# Revit family: КСК_без стены_Eng
name_source: partatom
category: Mechanical Equipment
units: mm (PartAtom-declared; Revit-internal decimal feet)

## family parameters
Always vertical = Yes
Classification = None
Cut with Voids When Loaded = No
Part Type = Normal
Room Calculation Point = No
Round Connector Dimension = Use Diameter
Shared = No
Work Plane-Based = No

## types (24) — shared parameters
00_20_Manufacturer = Vents
00_20_Name = Centrifugal kitchen fan in sound-insulated casing
Casing Material = Steel, galvanized
Frequency = 50 Hz
Load Classification = HVAC
Maintenance zone material = <By Category>
Manufacturer = Vents
URL = https://ventilation-system.com
zero-valued in all types: Default Elevation

## per-type parameters (varying)
- KSK 150 4D: Amperage=1 A; B=410 mm; D=150 mm  [stored 0.492126 ft]; Diameter=150 mm  [stored 0.492126 ft]; Dy=145 mm  [stored 0.475722 ft]; H=540 mm; H1=365 mm; Height=540 mm; L=525 mm; L1=500 mm; L4=205 mm; Length=525 mm; Maximum Air Flow=730.0 m³/h; Motor=Motor : Motor_0.25 kW; Number of Fase=3; Power=180 W; Sound pressure level at 3 m distance=41 dBA; Voltage=400 V; Weight=17.00 kg; Width=410 mm; b=105 mm  [stored 0.344488 ft]; h1=32 mm  [stored 0.104987 ft]; l1=50 mm  [stored 0.164042 ft]; l2=73 mm; l3=133 mm  [stored 0.436352 ft]
- KSK 150 4E: Amperage=2 A; B=410 mm; D=150 mm  [stored 0.492126 ft]; Diameter=150 mm  [stored 0.492126 ft]; Dy=145 mm  [stored 0.475722 ft]; H=540 mm; H1=365 mm; Height=540 mm; L=525 mm; L1=500 mm; L4=205 mm; Length=525 mm; Maximum Air Flow=700.0 m³/h; Motor=Motor : Motor_0.25 kW; Number of Fase=1; Power=180 W; Sound pressure level at 3 m distance=41 dBA; Voltage=230 V; Weight=17.00 kg; Width=410 mm; b=105 mm  [stored 0.344488 ft]; h1=32 mm  [stored 0.104987 ft]; l1=50 mm  [stored 0.164042 ft]; l2=73 mm; l3=133 mm  [stored 0.436352 ft]
- KSK 450 6E: Amperage=3 A; B=996 mm; D=450 mm; Diameter=450 mm; Dy=445 mm; H=980 mm; H1=870 mm; Height=980 mm; L=925 mm; L1=900 mm; L4=437 mm; Length=925 mm; Maximum Air Flow=5299.0 m³/h; Motor=Motor : Motor_0.55 kW; Number of Fase=1; Power=594 W; Sound pressure level at 3 m distance=50 dBA; Voltage=230 V; Weight=105.00 kg; Width=996 mm; b=255 mm  [stored 0.836614 ft]; h1=36 mm  [stored 0.11811 ft]; l1=65 mm  [stored 0.213255 ft]; l2=189 mm; l3=249 mm
- KSK 160 4D: Amperage=1 A; B=410 mm; D=160 mm  [stored 0.524934 ft]; Diameter=160 mm  [stored 0.524934 ft]; Dy=155 mm  [stored 0.50853 ft]; H=540 mm; H1=365 mm; Height=540 mm; L=525 mm; L1=500 mm; L4=205 mm; Length=525 mm; Maximum Air Flow=730.0 m³/h; Motor=Motor : Motor_0.25 kW; Number of Fase=3; Power=180 W; Sound pressure level at 3 m distance=41 dBA; Voltage=400 V; Weight=17.00 kg; Width=410 mm; b=110 mm  [stored 0.360892 ft]; h1=32 mm  [stored 0.104987 ft]; l1=50 mm  [stored 0.164042 ft]; l2=73 mm; l3=133 mm  [stored 0.436352 ft]
- KSK 160 4E: Amperage=2 A; B=410 mm; D=160 mm  [stored 0.524934 ft]; Diameter=160 mm  [stored 0.524934 ft]; Dy=155 mm  [stored 0.50853 ft]; H=540 mm; H1=365 mm; Height=540 mm; L=525 mm; L1=500 mm; L4=205 mm; Length=525 mm; Maximum Air Flow=700.0 m³/h; Motor=Motor : Motor_0.25 kW; Number of Fase=1; Power=180 W; Sound pressure level at 3 m distance=41 dBA; Voltage=230 V; Weight=17.00 kg; Width=410 mm; b=110 mm  [stored 0.360892 ft]; h1=32 mm  [stored 0.104987 ft]; l1=50 mm  [stored 0.164042 ft]; l2=73 mm; l3=133 mm  [stored 0.436352 ft]
- KSK 200 4D: Amperage=2 A; B=485 mm; D=200 mm  [stored 0.656168 ft]; Diameter=200 mm  [stored 0.656168 ft]; Dy=195 mm  [stored 0.639764 ft]; H=600 mm; H1=425 mm; Height=600 mm; L=625 mm; L1=600 mm; L4=235 mm  [stored 0.770997 ft]; Length=625 mm; Maximum Air Flow=1650.0 m³/h; Motor=Motor : Motor_0.75 kW; Number of Fase=3; Power=750 W; Sound pressure level at 3 m distance=45 dBA; Voltage=400 V; Weight=25.00 kg; Width=485 mm; b=130 mm  [stored 0.426509 ft]; h1=32 mm  [stored 0.104987 ft]; l1=50 mm  [stored 0.164042 ft]; l2=88 mm; l3=148 mm
- KSK 200 4E: Amperage=3 A; B=485 mm; D=200 mm  [stored 0.656168 ft]; Diameter=200 mm  [stored 0.656168 ft]; Dy=195 mm  [stored 0.639764 ft]; H=600 mm; H1=425 mm; Height=600 mm; L=625 mm; L1=600 mm; L4=235 mm  [stored 0.770997 ft]; Length=625 mm; Maximum Air Flow=1600.0 m³/h; Motor=Motor : Motor_0.55 kW; Number of Fase=1; Power=550 W; Sound pressure level at 3 m distance=45 dBA; Voltage=230 V; Weight=25.00 kg; Width=485 mm; b=130 mm  [stored 0.426509 ft]; h1=32 mm  [stored 0.104987 ft]; l1=50 mm  [stored 0.164042 ft]; l2=88 mm; l3=148 mm
- KSK 250 4D: Amperage=3 A; B=575 mm; D=250 mm  [stored 0.82021 ft]; Diameter=250 mm  [stored 0.82021 ft]; Dy=245 mm  [stored 0.803806 ft]; H=665 mm; H1=505 mm; Height=665 mm; L=700 mm; L1=675 mm; L4=285 mm  [stored 0.935039 ft]; Length=700 mm; Maximum Air Flow=3500.0 m³/h; Motor=Motor : Motor_1.5 kW; Number of Fase=3; Power=1500 W; Sound pressure level at 3 m distance=51 dBA; Voltage=400 V; Weight=40.00 kg; Width=575 mm; b=155 mm  [stored 0.50853 ft]; h1=32 mm  [stored 0.104987 ft]; l1=50 mm  [stored 0.164042 ft]; l2=113 mm  [stored 0.370735 ft]; l3=173 mm
- KSK 250 4E: Amperage=11 A; B=575 mm; D=250 mm  [stored 0.82021 ft]; Diameter=250 mm  [stored 0.82021 ft]; Dy=245 mm  [stored 0.803806 ft]; H=665 mm; H1=505 mm; Height=665 mm; L=700 mm; L1=675 mm; L4=285 mm  [stored 0.935039 ft]; Length=700 mm; Maximum Air Flow=3400.0 m³/h; Motor=Motor : Motor_1.5 kW; Number of Fase=1; Power=1500 W; Sound pressure level at 3 m distance=51 dBA; Voltage=230 V; Weight=40.00 kg; Width=575 mm; b=155 mm  [stored 0.50853 ft]; h1=32 mm  [stored 0.104987 ft]; l1=50 mm  [stored 0.164042 ft]; l2=113 mm  [stored 0.370735 ft]; l3=173 mm
- KSK 315 2D: Amperage=3 A; B=690 mm; D=315 mm  [stored 1.03346 ft]; Diameter=315 mm  [stored 1.03346 ft]; Dy=310 mm  [stored 1.01706 ft]; H=708 mm; H1=600 mm; Height=708 mm; L=715 mm; L1=700 mm; L4=327 mm; Length=715 mm; Maximum Air Flow=5290.0 m³/h; Motor=Motor : Motor_2.2 kW; Number of Fase=3; Power=2011 W; Sound pressure level at 3 m distance=54 dBA; Voltage=400 V; Weight=60.00 kg; Width=690 mm; b=188 mm; h1=32 mm  [stored 0.104987 ft]; l1=50 mm  [stored 0.164042 ft]; l2=134 mm; l3=194 mm
- KSK 315 2E: Amperage=12 A; B=690 mm; D=315 mm  [stored 1.03346 ft]; Diameter=315 mm  [stored 1.03346 ft]; Dy=310 mm  [stored 1.01706 ft]; H=708 mm; H1=600 mm; Height=708 mm; L=715 mm; L1=700 mm; L4=327 mm; Length=715 mm; Maximum Air Flow=5345.0 m³/h; Motor=Motor : Motor_3 kW; Number of Fase=1; Power=2816 W; Sound pressure level at 3 m distance=55 dBA; Voltage=230 V; Weight=61.00 kg; Width=690 mm; b=188 mm; h1=32 mm  [stored 0.104987 ft]; l1=50 mm  [stored 0.164042 ft]; l2=134 mm; l3=194 mm
- KSK 315 4D: Amperage=1 A; B=690 mm; D=315 mm  [stored 1.03346 ft]; Diameter=315 mm  [stored 1.03346 ft]; Dy=310 mm  [stored 1.01706 ft]; H=708 mm; H1=600 mm; Height=708 mm; L=715 mm; L1=700 mm; L4=327 mm; Length=715 mm; Maximum Air Flow=2355.0 m³/h; Motor=Motor : Motor_0.25 kW; Number of Fase=3; Power=206 W; Sound pressure level at 3 m distance=48 dBA; Voltage=400 V; Weight=52.00 kg; Width=690 mm; b=188 mm; h1=32 mm  [stored 0.104987 ft]; l1=50 mm  [stored 0.164042 ft]; l2=134 mm; l3=194 mm
- KSK 315 4E: Amperage=2 A; B=690 mm; D=315 mm  [stored 1.03346 ft]; Diameter=315 mm  [stored 1.03346 ft]; Dy=310 mm  [stored 1.01706 ft]; H=708 mm; H1=600 mm; Height=708 mm; L=715 mm; L1=700 mm; L4=327 mm; Length=715 mm; Maximum Air Flow=2310.0 m³/h; Motor=Motor : Motor_0.37 kW; Number of Fase=1; Power=383 W; Sound pressure level at 3 m distance=47 dBA; Voltage=230 V; Weight=53.00 kg; Width=690 mm; b=188 mm; h1=32 mm  [stored 0.104987 ft]; l1=50 mm  [stored 0.164042 ft]; l2=134 mm; l3=194 mm
- KSK 355 2D: Amperage=6 A; B=740 mm; D=355 mm; Diameter=355 mm; Dy=350 mm; H=764 mm; H1=655 mm; Height=764 mm; L=727 mm; L1=700 mm; L4=352 mm; Length=727 mm; Maximum Air Flow=6185.0 m³/h; Motor=Motor : Motor_3 kW; Number of Fase=3; Power=3145 W; Sound pressure level at 3 m distance=54 dBA; Voltage=400 V; Weight=65.00 kg; Width=740 mm; b=208 mm; h1=36 mm  [stored 0.11811 ft]; l1=65 mm  [stored 0.213255 ft]; l2=146 mm  [stored 0.479003 ft]; l3=206 mm  [stored 0.675853 ft]
- KSK 355 2E: Amperage=13 A; B=740 mm; D=355 mm; Diameter=355 mm; Dy=350 mm; H=764 mm; H1=655 mm; Height=764 mm; L=727 mm; L1=700 mm; L4=352 mm; Length=727 mm; Maximum Air Flow=6570.0 m³/h; Motor=Motor : Motor_2.2 kW; Number of Fase=1; Power=2621 W; Sound pressure level at 3 m distance=54 dBA; Voltage=230 V; Weight=68.00 kg; Width=740 mm; b=208 mm; h1=36 mm  [stored 0.11811 ft]; l1=65 mm  [stored 0.213255 ft]; l2=146 mm  [stored 0.479003 ft]; l3=206 mm  [stored 0.675853 ft]
- KSK 355 4D: Amperage=1 A; B=740 mm; D=355 mm; Diameter=355 mm; Dy=350 mm; H=764 mm; H1=655 mm; Height=764 mm; L=727 mm; L1=700 mm; L4=352 mm; Length=727 mm; Maximum Air Flow=3270.0 m³/h; Motor=Motor : Motor_0.55 kW; Number of Fase=3; Power=580 W; Sound pressure level at 3 m distance=50 dBA; Voltage=400 V; Weight=59.00 kg; Width=740 mm; b=208 mm; h1=36 mm  [stored 0.11811 ft]; l1=65 mm  [stored 0.213255 ft]; l2=146 mm  [stored 0.479003 ft]; l3=206 mm  [stored 0.675853 ft]
- KSK 355 4E: Amperage=2 A; B=740 mm; D=355 mm; Diameter=355 mm; Dy=350 mm; H=764 mm; H1=655 mm; Height=764 mm; L=727 mm; L1=700 mm; L4=352 mm; Length=727 mm; Maximum Air Flow=3860.0 m³/h; Motor=Motor : Motor_0.55 kW; Number of Fase=1; Power=525 W; Sound pressure level at 3 m distance=52 dBA; Voltage=230 V; Weight=60.00 kg; Width=740 mm; b=208 mm; h1=36 mm  [stored 0.11811 ft]; l1=65 mm  [stored 0.213255 ft]; l2=146 mm  [stored 0.479003 ft]; l3=206 mm  [stored 0.675853 ft]
- KSK 400 4D: Amperage=2 A; B=906 mm; D=400 mm; Diameter=400 mm; Dy=395 mm; H=900 mm; H1=790 mm; Height=900 mm; L=908 mm; L1=900 mm; L4=402 mm; Length=908 mm; Maximum Air Flow=5098.0 m³/h; Motor=Motor : Motor_0.75 kW; Number of Fase=3; Power=785 W; Sound pressure level at 3 m distance=53 dBA; Voltage=400 V; Weight=92.00 kg; Width=906 mm; b=230 mm  [stored 0.754593 ft]; h1=36 mm  [stored 0.11811 ft]; l1=65 mm  [stored 0.213255 ft]; l2=171 mm  [stored 0.561024 ft]; l3=231 mm  [stored 0.757874 ft]
- KSK 400 4E: Amperage=5 A; B=906 mm; D=400 mm; Diameter=400 mm; Dy=395 mm; H=900 mm; H1=790 mm; Height=900 mm; L=908 mm; L1=900 mm; L4=402 mm; Length=908 mm; Maximum Air Flow=5392.0 m³/h; Motor=Motor : Motor_1.1 kW; Number of Fase=1; Power=1048 W; Sound pressure level at 3 m distance=54 dBA; Voltage=230 V; Weight=92.00 kg; Width=906 mm; b=230 mm  [stored 0.754593 ft]; h1=36 mm  [stored 0.11811 ft]; l1=65 mm  [stored 0.213255 ft]; l2=171 mm  [stored 0.561024 ft]; l3=231 mm  [stored 0.757874 ft]
- KSK 400 6D: Amperage=1 A; B=906 mm; D=400 mm; Diameter=400 mm; Dy=395 mm; H=900 mm; H1=790 mm; Height=900 mm; L=908 mm; L1=900 mm; L4=402 mm; Length=908 mm; Maximum Air Flow=2966.0 m³/h; Motor=Motor : Motor_0.37 kW; Number of Fase=3; Power=357 W; Sound pressure level at 3 m distance=47 dBA; Voltage=400 V; Weight=87.00 kg; Width=906 mm; b=230 mm  [stored 0.754593 ft]; h1=36 mm  [stored 0.11811 ft]; l1=65 mm  [stored 0.213255 ft]; l2=171 mm  [stored 0.561024 ft]; l3=231 mm  [stored 0.757874 ft]
- KSK 400 6E: Amperage=2 A; B=906 mm; D=400 mm; Diameter=400 mm; Dy=395 mm; H=900 mm; H1=790 mm; Height=900 mm; L=908 mm; L1=900 mm; L4=402 mm; Length=908 mm; Maximum Air Flow=2915.0 m³/h; Motor=Motor : Motor_0.37 kW; Number of Fase=1; Power=362 W; Sound pressure level at 3 m distance=48 dBA; Voltage=230 V; Weight=87.00 kg; Width=906 mm; b=230 mm  [stored 0.754593 ft]; h1=36 mm  [stored 0.11811 ft]; l1=65 mm  [stored 0.213255 ft]; l2=171 mm  [stored 0.561024 ft]; l3=231 mm  [stored 0.757874 ft]
- KSK 450 4D: Amperage=3 A; B=996 mm; D=450 mm; Diameter=450 mm; Dy=445 mm; H=980 mm; H1=870 mm; Height=980 mm; L=925 mm; L1=900 mm; L4=437 mm; Length=925 mm; Maximum Air Flow=7840.0 m³/h; Motor=Motor : Motor_1.5 kW; Number of Fase=3; Power=1350 W; Sound pressure level at 3 m distance=56 dBA; Voltage=400 V; Weight=109.00 kg; Width=996 mm; b=255 mm  [stored 0.836614 ft]; h1=36 mm  [stored 0.11811 ft]; l1=65 mm  [stored 0.213255 ft]; l2=189 mm; l3=249 mm
- KSK 450 4E: Amperage=7 A; B=996 mm; D=450 mm; Diameter=450 mm; Dy=445 mm; H=980 mm; H1=870 mm; Height=980 mm; L=925 mm; L1=900 mm; L4=437 mm; Length=925 mm; Maximum Air Flow=8138.0 m³/h; Motor=Motor : Motor_1.5 kW; Number of Fase=1; Power=1570 W; Sound pressure level at 3 m distance=57 dBA; Voltage=230 V; Weight=109.00 kg; Width=996 mm; b=255 mm  [stored 0.836614 ft]; h1=36 mm  [stored 0.11811 ft]; l1=65 mm  [stored 0.213255 ft]; l2=189 mm; l3=249 mm
- KSK 450 6D: Amperage=1 A; B=996 mm; D=450 mm; Diameter=450 mm; Dy=445 mm; H=980 mm; H1=870 mm; Height=980 mm; L=925 mm; L1=900 mm; L4=437 mm; Length=925 mm; Maximum Air Flow=4991.0 m³/h; Motor=Motor : Motor_0.55 kW; Number of Fase=3; Power=454 W; Sound pressure level at 3 m distance=49 dBA; Voltage=400 V; Weight=105.00 kg; Width=996 mm; b=255 mm  [stored 0.836614 ft]; h1=36 mm  [stored 0.11811 ft]; l1=65 mm  [stored 0.213255 ft]; l2=189 mm; l3=249 mm

note: column(s) folded — value = type name in every type: 00_20_Type

note: [stored X ft] marks values corroborated as IEEE doubles in the binary element streams (Revit-internal decimal feet)
